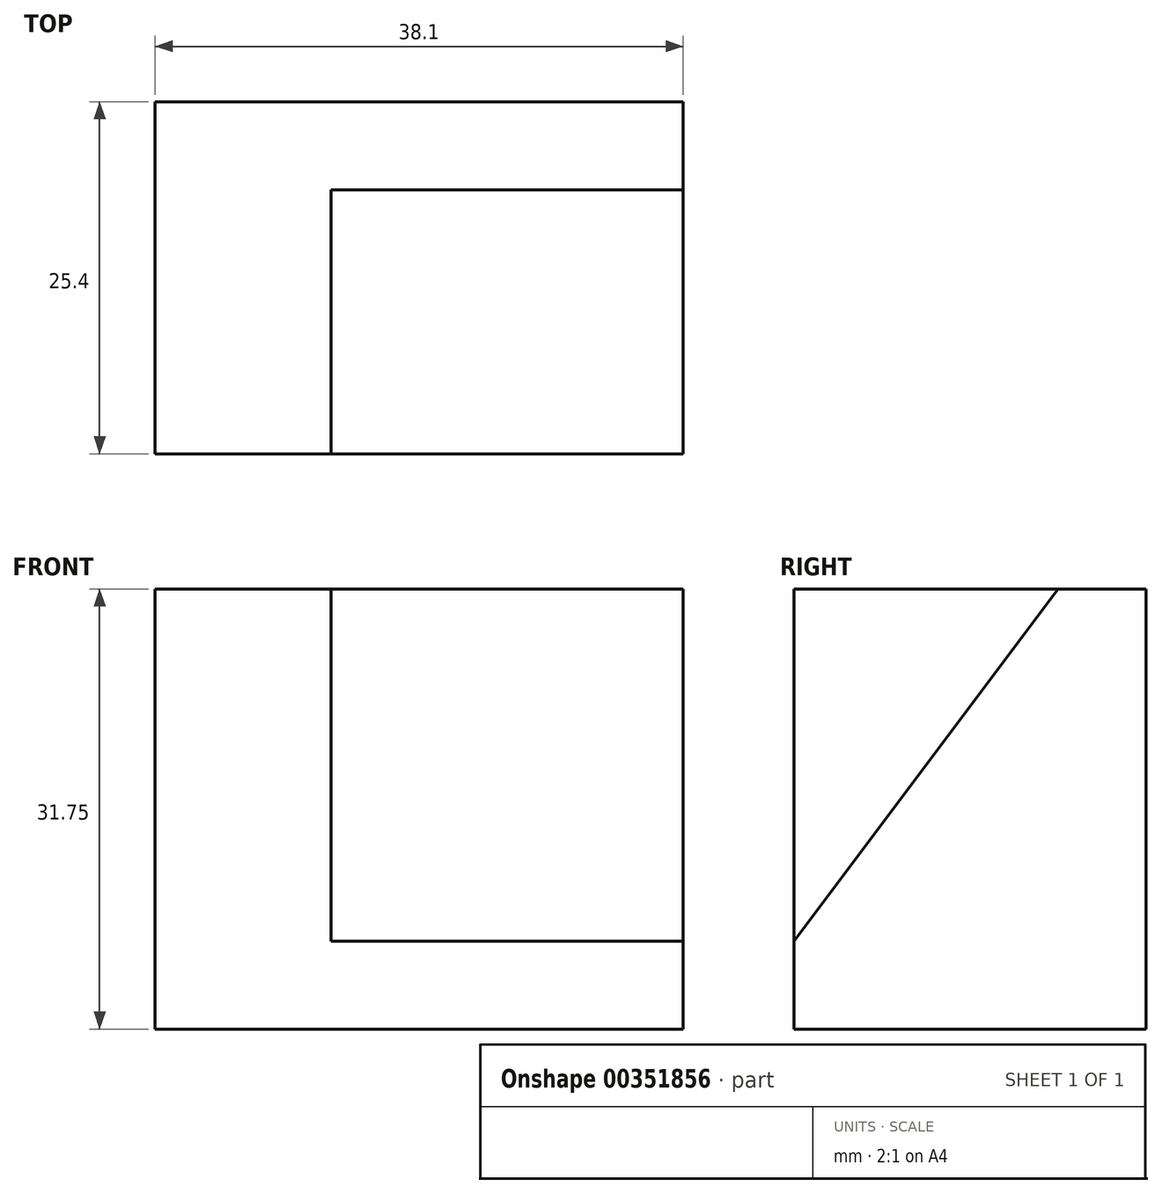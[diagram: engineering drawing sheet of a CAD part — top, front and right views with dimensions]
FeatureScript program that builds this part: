
annotation { "Feature Type Name" : "Feature", "Feature Type Description" : "" }
export const myFeature = defineFeature(function(context is Context, id is Id, definition is map)
    precondition{}
    {
        {
            var Q0;
            Q0=qCreatedBy(makeId("Right.planeOp"),FACE);
            var sketch = newSketch(context, id + "F0", { "sketchPlane" : qUnion([Q0])});
            skLineSegment(sketch, "E0", {"start": v(0, 0) * mm, "end": v(25.4, 0) * mm});
            skLineSegment(sketch, "E1", {"start": v(25.4, 0) * mm, "end": v(25.4, 31.75) * mm});
            skLineSegment(sketch, "E2", {"start": v(25.4, 31.75) * mm, "end": v(0, 31.75) * mm});
            skLineSegment(sketch, "E3", {"start": v(0, 31.75) * mm, "end": v(0, 0) * mm});
            skSolve(sketch);
        }
        {
            var Q0;
            Q0=makeQuery(id+"F0.imprint","IMPRINT",FACE,{"disambiguationData":[TD([[makeQuery(id+"F0.imprint","IMPRINT",EDGE,{"derivedFrom":sQuery(id+"F0.wireOp",EDGE,"E0")}),1.0]])]});
            extrude(context, id + "F1", {"entities" : qUnion([Q0]), "depth" : 38.1 * mm});
        }
        {
            var Q0;
            Q0=makeQuery(id+"F1.opExtrude","CAP_FACE",FACE,{"disambiguationData":[OSD([sQuery(id+"F0.wireOp",EDGE,"E0"),sQuery(id+"F0.wireOp",EDGE,"E1"),sQuery(id+"F0.wireOp",EDGE,"E2"),sQuery(id+"F0.wireOp",EDGE,"E3")])],"isStart":false});
            var sketch = newSketch(context, id + "F2", { "sketchPlane" : qUnion([Q0])});
            skLineSegment(sketch, "E4", {"start": v(0, 6.35) * mm, "end": v(19.05, 31.75) * mm});
            skSolve(sketch);
        }
        {
            var Q0;
            {var subQ0=sQuery(id+"F2.wireOp",EDGE,"E4");Q0=makeQuery(id+"F2.imprint","IMPRINT",FACE,{"disambiguationData":[TD([[makeQuery(id+"F2.imprint","IMPRINT",EDGE,{"derivedFrom":subQ0}),1.0]])]});}
            extrude(context, id + "F3", {"entities" : qUnion([Q0]), "operationType" : NewBodyOperationType.REMOVE, "oppositeDirection" : true, "depth" : 25.4 * mm});
        }
    });
